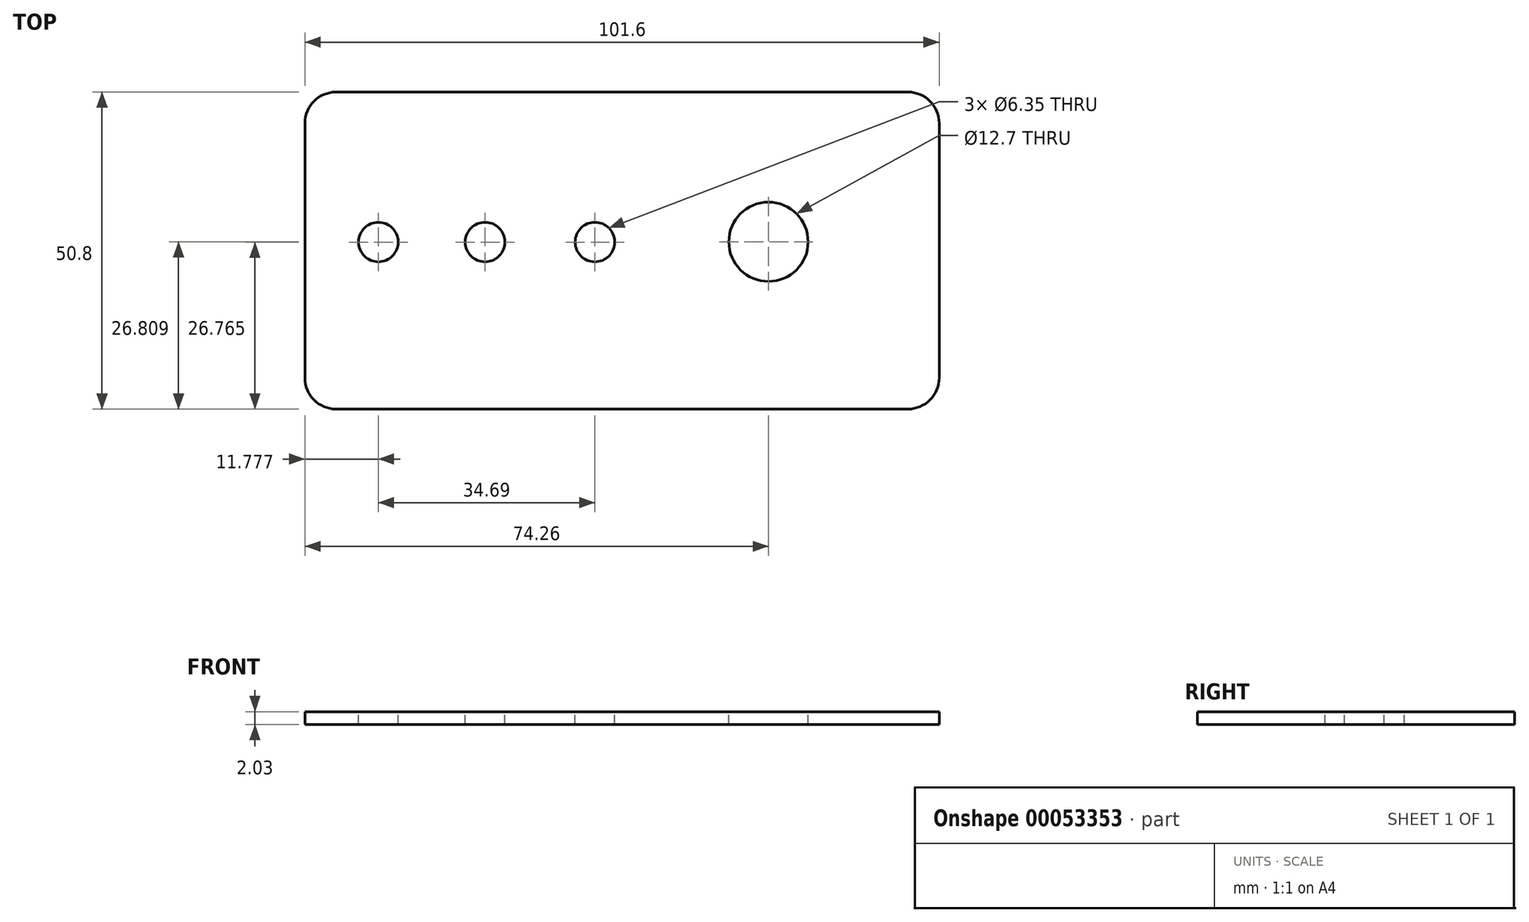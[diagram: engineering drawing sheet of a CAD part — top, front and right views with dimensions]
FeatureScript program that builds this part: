
annotation { "Feature Type Name" : "Feature", "Feature Type Description" : "" }
export const myFeature = defineFeature(function(context is Context, id is Id, definition is map)
    precondition{}
    {
        {
            var Q0;
            Q0=qCreatedBy(makeId("Top.planeOp"),FACE);
            var sketch = newSketch(context, id + "F0", { "sketchPlane" : qUnion([Q0])});
            skLineSegment(sketch, "E0.bottom", {"start": v(-52.16, 30.28) * mm, "end": v(49.44, 30.28) * mm});
            skLineSegment(sketch, "E0.top", {"start": v(-52.16, -20.52) * mm, "end": v(49.44, -20.52) * mm});
            skLineSegment(sketch, "E0.left", {"start": v(-52.16, 30.28) * mm, "end": v(-52.16, -20.52) * mm});
            skLineSegment(sketch, "E0.right", {"start": v(49.44, 30.28) * mm, "end": v(49.44, -20.52) * mm});
            skSolve(sketch);
        }
        {
            var Q0;
            Q0=makeQuery(id+"F0.imprint","IMPRINT",FACE,{"disambiguationData":[TD([[makeQuery(id+"F0.imprint","IMPRINT",EDGE,{"derivedFrom":sQuery(id+"F0.wireOp",EDGE,"E0.bottom")}),-1.0]])]});
            extrude(context, id + "F1", {"entities" : qUnion([Q0]), "depth" : 2.03 * mm});
        }
        {
            var Q0;
            Q0=makeQuery(id+"F1.opExtrude","SWEPT_EDGE",EDGE,{"disambiguationData":[OSD([sQuery(id+"F0.wireOp",EDGE,"E0.bottom"),sQuery(id+"F0.wireOp",EDGE,"E0.left")])]});
            var Q1;
            Q1=makeQuery(id+"F1.opExtrude","SWEPT_EDGE",EDGE,{"disambiguationData":[OSD([sQuery(id+"F0.wireOp",EDGE,"E0.bottom"),sQuery(id+"F0.wireOp",EDGE,"E0.right")])]});
            var Q2;
            Q2=makeQuery(id+"F1.opExtrude","SWEPT_EDGE",EDGE,{"disambiguationData":[OSD([sQuery(id+"F0.wireOp",EDGE,"E0.top"),sQuery(id+"F0.wireOp",EDGE,"E0.left")])]});
            var Q3;
            Q3=makeQuery(id+"F1.opExtrude","SWEPT_EDGE",EDGE,{"disambiguationData":[OSD([sQuery(id+"F0.wireOp",EDGE,"E0.top"),sQuery(id+"F0.wireOp",EDGE,"E0.right")])]});
            fillet(context, id + "F2", {"entities" : qUnion([Q0, Q1, Q2, Q3]), "radius" : 5 * mm, "tangentPropagation" : true, "allowEdgeOverflow" : false});
        }
        {
            var Q0;
            Q0=makeQuery(id+"F1.opExtrude","CAP_FACE",FACE,{"disambiguationData":[OSD([sQuery(id+"F0.wireOp",EDGE,"E0.bottom"),sQuery(id+"F0.wireOp",EDGE,"E0.top"),sQuery(id+"F0.wireOp",EDGE,"E0.left"),sQuery(id+"F0.wireOp",EDGE,"E0.right")])],"isStart":false});
            var sketch = newSketch(context, id + "F3", { "sketchPlane" : qUnion([Q0])});
            skPoint(sketch, "E1", {"position": v(-40.38, 6.25) * mm});
            skPoint(sketch, "E2", {"position": v(-23.3, 6.25) * mm});
            skPoint(sketch, "E3", {"position": v(-5.7, 6.25) * mm});
            skSolve(sketch);
        }
        {
            var Q0;
            Q0=sQuery(id+"F3.wireOp",VERTEX,"E1");
            var Q1;
            Q1=sQuery(id+"F3.wireOp",VERTEX,"E2");
            var Q2;
            Q2=sQuery(id+"F3.wireOp",VERTEX,"E3");
            var Q3;
            Q3=makeQuery(id+"F1.opExtrude","SWEPT_BODY",BODY,{"disambiguationData":[OSD([sQuery(id+"F0.wireOp",EDGE,"E0.bottom"),sQuery(id+"F0.wireOp",EDGE,"E0.top"),sQuery(id+"F0.wireOp",EDGE,"E0.left"),sQuery(id+"F0.wireOp",EDGE,"E0.right")])]});
            hole(context, id + "F4", {"style" : HoleStyle.SIMPLE, "holeDiameter" : 6.35 * mm, "endStyle" : HoleEndStyle.THROUGH, "locations" : qUnion([Q0, Q1, Q2]), "scope" : qUnion([Q3])});
        }
        {
            var Q0;
            Q0=makeQuery(id+"F1.opExtrude","CAP_FACE",FACE,{"disambiguationData":[OSD([sQuery(id+"F0.wireOp",EDGE,"E0.bottom"),sQuery(id+"F0.wireOp",EDGE,"E0.top"),sQuery(id+"F0.wireOp",EDGE,"E0.left"),sQuery(id+"F0.wireOp",EDGE,"E0.right")])],"isStart":false});
            var sketch = newSketch(context, id + "F5", { "sketchPlane" : qUnion([Q0])});
            skPoint(sketch, "E4", {"position": v(22.1, 6.29) * mm});
            skSolve(sketch);
        }
        {
            var Q0;
            Q0=sQuery(id+"F5.wireOp",VERTEX,"E4");
            var Q1;
            Q1=makeQuery(id+"F1.opExtrude","SWEPT_BODY",BODY,{"disambiguationData":[OSD([sQuery(id+"F0.wireOp",EDGE,"E0.bottom"),sQuery(id+"F0.wireOp",EDGE,"E0.top"),sQuery(id+"F0.wireOp",EDGE,"E0.left"),sQuery(id+"F0.wireOp",EDGE,"E0.right")])]});
            hole(context, id + "F6", {"style" : HoleStyle.SIMPLE, "holeDiameter" : 12.7 * mm, "endStyle" : HoleEndStyle.THROUGH, "locations" : qUnion([Q0]), "scope" : qUnion([Q1])});
        }
    });
